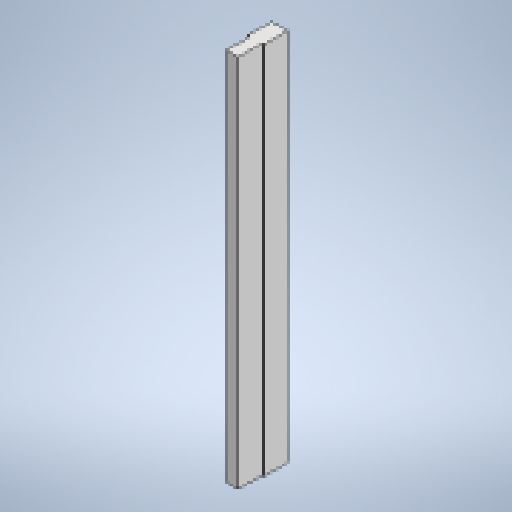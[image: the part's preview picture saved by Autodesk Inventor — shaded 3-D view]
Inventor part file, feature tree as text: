
AUTODESK INVENTOR PART (.ipt)
format: ipt  version: 2025.1 (Build 291241020, 241B)  size: 142,336 bytes
history: native  units: mm
features: extrude x1, sketch x1
ambient origin geometry x8: Origin, YZ Plane, XZ Plane, XY Plane, X Axis, Y Axis, Z Axis, Center Point
bodies: Solid1 (feature_tree)
feature tree (2):
  extrude  "Extrusion1"  Depth=30.0mm
  sketch  "Sketch1"  dims[d0=20.0mm d1=30.0mm d2=15.0mm d3=30.0mm d4=476.0mm d5=0.0mm]
